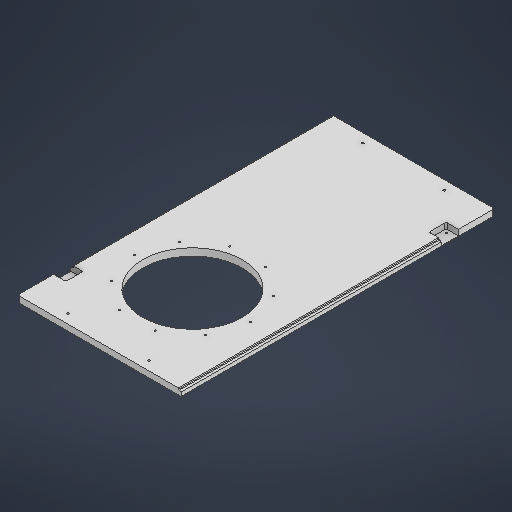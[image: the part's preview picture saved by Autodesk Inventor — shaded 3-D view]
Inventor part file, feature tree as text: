
AUTODESK INVENTOR PART (.ipt)
format: ipt  version: 2025 (Build 290162000, 162)  size: 326,144 bytes
history: native  units: in
note: dims shown in document units (in); Inventor stores cm internally (conversion verified against a paired STEP export)
features: sketch x9, chamfer x5, extrude x4, hole x3, plane x2, fillet x1
ambient origin geometry x8: Origin, YZ Plane, XZ Plane, XY Plane, X Axis, Y Axis, Z Axis, Center Point
bodies: Solid1 (feature_tree)
feature tree (24):
  extrude  "Extrusion1"  Depth=27.1654in
  sketch  "Sketch2"  dims[d2=0.625in d3=0.0in d4=8.0709in]
  extrude  "Extrusion2"  Depth=0.625in
  plane  "Work Plane1"
  hole  "Hole3"  [1 undecoded]
  sketch  "Sketch7"  dims[d56=25.5906in]
  plane  "Work Plane2"
  hole  "Hole4"  [1 undecoded]
  sketch  "Sketch9"  dims[d64=10.3543in]
  fillet  "Fillet2"  Radius=7.0625in
  chamfer  "Chamfer1"  Distance=0.1575in
  chamfer  "Chamfer2"  Distance=3.937in Angle=360.0deg
  extrude  "Extrusion7"  Depth=1.063in
  extrude  "Extrusion8"  Depth=1.063in
  chamfer  "Chamfer3"  Distance=1.4961in
  chamfer  "Chamfer4"  Distance=1.4961in
  hole  "Hole5"  [1 undecoded]
  chamfer  "Chamfer5"  Distance=3.1102in
  sketch  "Sketch1"  dims[d0=14.1732in d1=27.1654in]
  sketch  "Sketch6"  dims[d8=10.6299in d50=5.9055in d55=7.0625in]
  sketch  "Sketch8"  dims[d57=0.1936in d58=0.1969in d59=0.1575in d60=0.0787in d61=90.0deg d62=0.1969in d63=0.8108in]
  sketch  "Sketch Circular Pattern4"  dims[d5=8.6614in d6=0.0in d7=0.0in]
  sketch  "Sketch10"  dims[d65=10.6299in]
  sketch  "Sketch11"  dims[d68=10.0394in d69=0.1575in d70=3.937in d72=360.0deg d74=0.1628in d75=0.3937in d76=0.1575in d77=0.0787in d78=90.0deg d79=0.3937in d80=0.8108in d82=1.063in d83=1.063in d84=1.4961in d85=1.4961in d86=3.1102in d87=3.1102in d88=0.1969in d89=0.0984in d90=0.0787in d91=45.0deg d92=0.0984in d93=0.0787in d94=45.0deg d95=0.1181in d96=0.1181in d97=0.4951in d98=0.0in d99=0.2362in d100=0.2362in d101=0.122in d102=0.0in d103=0.0787in d104=0.1378in d105=45.0deg d106=0.1378in d107=0.0787in d108=45.0deg d109=0.748in d110=0.315in d111=0.8661in d112=0.748in d113=0.1299in d114=0.1299in d115=0.1299in d116=0.1299in d118=0.315in d119=0.8661in d120=0.748in d121=0.748in d122=0.1276in d123=0.315in d124=0.1575in d125=0.0787in d126=90.0deg d127=0.315in d128=0.8108in d129=0.0138in d130=0.0787in d131=45.0deg d26=0.0394in d27=0.0394in d28=0.0394in d29=0.0059in d30=0.0098in d31=0.0148in d32=0.5635in d33=0.0295in d34=0.8108in d35=0.0025in d36=0.0295in d37=0.0148in d66=0.0197in d67=0.0344in]
note: 3 required parameter values undecoded (feature->parameter linkage not recoverable at this tier; creation-order binding heuristic only, values carry confidence <= 0.55)
